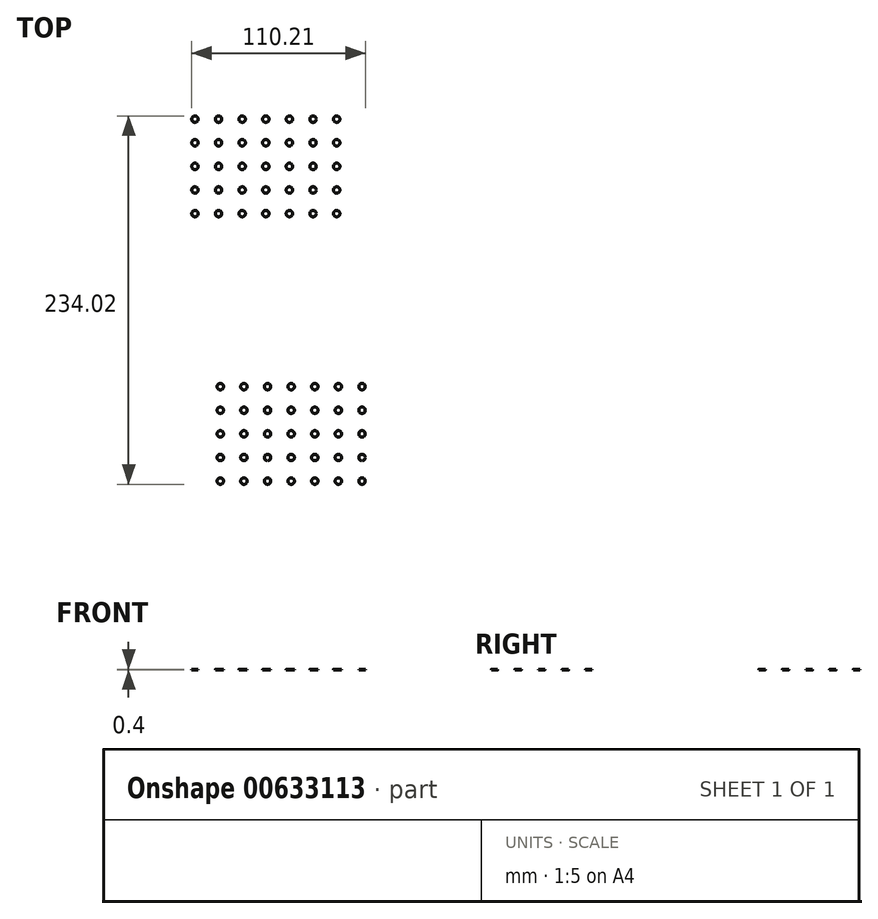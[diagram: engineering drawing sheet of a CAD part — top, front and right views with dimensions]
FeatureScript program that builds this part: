
annotation { "Feature Type Name" : "Feature", "Feature Type Description" : "" }
export const myFeature = defineFeature(function(context is Context, id is Id, definition is map)
    precondition{}
    {
        {
            var Q0;
            Q0=qCreatedBy(makeId("Top.planeOp"),FACE);
            var sketch = newSketch(context, id + "F0", { "sketchPlane" : qUnion([Q0])});
            skLineSegment(sketch, "E0.bottom", {"start": v(-80.56, 57.72) * mm, "end": v(79.44, 57.72) * mm});
            skLineSegment(sketch, "E0.right", {"start": v(79.44, 57.72) * mm, "end": v(79.44, -47.28) * mm});
            skCircle(sketch, "E1", {"center": v(-45.56, -24.78) * mm, "radius": 2.05 * mm});
            skCircle(sketch, "E2.0.1.0", {"center": v(-45.56, -9.78) * mm, "radius": 2.05 * mm});
            skCircle(sketch, "E2.0.2.0", {"center": v(-45.56, 5.22) * mm, "radius": 2.05 * mm});
            skCircle(sketch, "E2.0.3.0", {"center": v(-45.56, 20.22) * mm, "radius": 2.05 * mm});
            skCircle(sketch, "E2.1.0.0", {"center": v(-30.56, -24.78) * mm, "radius": 2.05 * mm});
            skCircle(sketch, "E2.1.1.0", {"center": v(-30.56, -9.78) * mm, "radius": 2.05 * mm});
            skCircle(sketch, "E2.1.2.0", {"center": v(-30.56, 5.22) * mm, "radius": 2.05 * mm});
            skCircle(sketch, "E2.1.3.0", {"center": v(-30.56, 20.22) * mm, "radius": 2.05 * mm});
            skCircle(sketch, "E2.2.0.0", {"center": v(-15.56, -24.78) * mm, "radius": 2.05 * mm});
            skCircle(sketch, "E2.2.1.0", {"center": v(-15.56, -9.78) * mm, "radius": 2.05 * mm});
            skCircle(sketch, "E2.2.2.0", {"center": v(-15.56, 5.22) * mm, "radius": 2.05 * mm});
            skCircle(sketch, "E2.2.3.0", {"center": v(-15.56, 20.22) * mm, "radius": 2.05 * mm});
            skCircle(sketch, "E2.3.0.0", {"center": v(-0.56, -24.78) * mm, "radius": 2.05 * mm});
            skCircle(sketch, "E2.3.1.0", {"center": v(-0.56, -9.78) * mm, "radius": 2.05 * mm});
            skCircle(sketch, "E2.3.2.0", {"center": v(-0.56, 5.22) * mm, "radius": 2.05 * mm});
            skCircle(sketch, "E2.3.3.0", {"center": v(-0.56, 20.22) * mm, "radius": 2.05 * mm});
            skCircle(sketch, "E2.4.0.0", {"center": v(14.44, -24.78) * mm, "radius": 2.05 * mm});
            skCircle(sketch, "E2.4.1.0", {"center": v(14.44, -9.78) * mm, "radius": 2.05 * mm});
            skCircle(sketch, "E2.4.2.0", {"center": v(14.44, 5.22) * mm, "radius": 2.05 * mm});
            skCircle(sketch, "E2.4.3.0", {"center": v(14.44, 20.22) * mm, "radius": 2.05 * mm});
            skCircle(sketch, "E2.5.0.0", {"center": v(29.44, -24.78) * mm, "radius": 2.05 * mm});
            skCircle(sketch, "E2.5.1.0", {"center": v(29.44, -9.78) * mm, "radius": 2.05 * mm});
            skCircle(sketch, "E2.5.2.0", {"center": v(29.44, 5.22) * mm, "radius": 2.05 * mm});
            skCircle(sketch, "E2.5.3.0", {"center": v(29.44, 20.22) * mm, "radius": 2.05 * mm});
            skCircle(sketch, "E2.6.0.0", {"center": v(44.44, -24.78) * mm, "radius": 2.05 * mm});
            skCircle(sketch, "E2.6.1.0", {"center": v(44.44, -9.78) * mm, "radius": 2.05 * mm});
            skCircle(sketch, "E2.6.2.0", {"center": v(44.44, 5.22) * mm, "radius": 2.05 * mm});
            skCircle(sketch, "E2.6.3.0", {"center": v(44.44, 20.22) * mm, "radius": 2.05 * mm});
            skLineSegment(sketch, "E2.direction1", {"start": v(-45.56, -24.78) * mm, "end": v(-30.56, -24.78) * mm, "construction": true});
            skLineSegment(sketch, "E2.direction2", {"start": v(-45.56, -24.78) * mm, "end": v(-45.56, -9.78) * mm, "construction": true});
            skCircle(sketch, "E3.0.0.4", {"center": v(-45.56, 35.22) * mm, "radius": 2.05 * mm});
            skCircle(sketch, "E3.0.1.4", {"center": v(-30.56, 35.22) * mm, "radius": 2.05 * mm});
            skCircle(sketch, "E3.0.2.4", {"center": v(-15.56, 35.22) * mm, "radius": 2.05 * mm});
            skCircle(sketch, "E3.0.3.4", {"center": v(-0.56, 35.22) * mm, "radius": 2.05 * mm});
            skCircle(sketch, "E3.0.4.4", {"center": v(14.44, 35.22) * mm, "radius": 2.05 * mm});
            skCircle(sketch, "E3.0.5.4", {"center": v(29.44, 35.22) * mm, "radius": 2.05 * mm});
            skCircle(sketch, "E3.0.6.4", {"center": v(44.44, 35.22) * mm, "radius": 2.05 * mm});
            skCircle(sketch, "E4", {"center": v(-70.56, 52.22) * mm, "radius": 1.55 * mm});
            skCircle(sketch, "E5", {"center": v(69.44, 52.22) * mm, "radius": 1.55 * mm});
            skCircle(sketch, "E6", {"center": v(-52.56, 52.22) * mm, "radius": 1.55 * mm});
            skCircle(sketch, "E7", {"center": v(51.44, 52.22) * mm, "radius": 1.55 * mm});
            skCircle(sketch, "E8", {"center": v(-45.56, 52.22) * mm, "radius": 2.6 * mm});
            skCircle(sketch, "E9", {"center": v(-0.56, 52.22) * mm, "radius": 2.6 * mm});
            skCircle(sketch, "E10", {"center": v(44.44, 52.22) * mm, "radius": 2.55 * mm});
            skCircle(sketch, "E11.MirrorC", {"center": v(-0.56, -41.78) * mm, "radius": 2.6 * mm});
            skCircle(sketch, "E12.MirrorC", {"center": v(51.44, -41.78) * mm, "radius": 1.55 * mm});
            skCircle(sketch, "E13.MirrorC", {"center": v(-52.56, -41.78) * mm, "radius": 1.55 * mm});
            skCircle(sketch, "E14.MirrorC", {"center": v(-45.56, -41.78) * mm, "radius": 2.6 * mm});
            skCircle(sketch, "E15.MirrorC", {"center": v(44.44, -41.78) * mm, "radius": 2.55 * mm});
            skCircle(sketch, "E16.MirrorC", {"center": v(69.44, -41.78) * mm, "radius": 1.55 * mm});
            skCircle(sketch, "E17.MirrorC", {"center": v(-70.56, -41.78) * mm, "radius": 1.55 * mm});
            skLineSegment(sketch, "E18.bottom", {"start": v(-64.45, -112.2) * mm, "end": v(95.55, -112.2) * mm});
            skLineSegment(sketch, "E18.right", {"start": v(95.55, -112.2) * mm, "end": v(95.55, -217.2) * mm});
            skCircle(sketch, "E19", {"center": v(-54.45, -117.7) * mm, "radius": 3 * mm});
            skCircle(sketch, "E20", {"center": v(85.55, -117.7) * mm, "radius": 3 * mm});
            skCircle(sketch, "E21", {"center": v(-36.45, -117.7) * mm, "radius": 1.55 * mm});
            skCircle(sketch, "E22", {"center": v(67.55, -117.7) * mm, "radius": 1.55 * mm});
            skCircle(sketch, "E23", {"center": v(-29.45, -117.7) * mm, "radius": 2.6 * mm});
            skCircle(sketch, "E24", {"center": v(15.55, -117.7) * mm, "radius": 2.6 * mm});
            skCircle(sketch, "E25", {"center": v(60.55, -117.7) * mm, "radius": 2.55 * mm});
            skLineSegment(sketch, "E26", {"start": v(95.55, -217.2) * mm, "end": v(15.55, -217.2) * mm});
            skCircle(sketch, "E27.MirrorC", {"center": v(15.55, -211.7) * mm, "radius": 2.6 * mm});
            skCircle(sketch, "E28.MirrorC", {"center": v(67.55, -211.7) * mm, "radius": 1.55 * mm});
            skCircle(sketch, "E29.MirrorC", {"center": v(-36.45, -211.7) * mm, "radius": 1.55 * mm});
            skCircle(sketch, "E30.MirrorC", {"center": v(-29.45, -211.7) * mm, "radius": 2.6 * mm});
            skCircle(sketch, "E31.MirrorC", {"center": v(60.55, -211.7) * mm, "radius": 2.55 * mm});
            skCircle(sketch, "E32.MirrorC", {"center": v(85.55, -211.7) * mm, "radius": 3 * mm});
            skCircle(sketch, "E33.MirrorC", {"center": v(-54.45, -211.7) * mm, "radius": 3 * mm});
            skCircle(sketch, "E34", {"center": v(-29.45, -194.7) * mm, "radius": 2.05 * mm});
            skCircle(sketch, "E35.0.1.0", {"center": v(-29.45, -179.7) * mm, "radius": 2.05 * mm});
            skCircle(sketch, "E35.0.2.0", {"center": v(-29.45, -164.7) * mm, "radius": 2.05 * mm});
            skCircle(sketch, "E35.0.3.0", {"center": v(-29.45, -149.7) * mm, "radius": 2.05 * mm});
            skCircle(sketch, "E35.1.0.0", {"center": v(-14.45, -194.7) * mm, "radius": 2.05 * mm});
            skCircle(sketch, "E35.1.1.0", {"center": v(-14.45, -179.7) * mm, "radius": 2.05 * mm});
            skCircle(sketch, "E35.1.2.0", {"center": v(-14.45, -164.7) * mm, "radius": 2.05 * mm});
            skCircle(sketch, "E35.1.3.0", {"center": v(-14.45, -149.7) * mm, "radius": 2.05 * mm});
            skCircle(sketch, "E35.2.0.0", {"center": v(0.55, -194.7) * mm, "radius": 2.05 * mm});
            skCircle(sketch, "E35.2.1.0", {"center": v(0.55, -179.7) * mm, "radius": 2.05 * mm});
            skCircle(sketch, "E35.2.2.0", {"center": v(0.55, -164.7) * mm, "radius": 2.05 * mm});
            skCircle(sketch, "E35.2.3.0", {"center": v(0.55, -149.7) * mm, "radius": 2.05 * mm});
            skCircle(sketch, "E35.3.0.0", {"center": v(15.55, -194.7) * mm, "radius": 2.05 * mm});
            skCircle(sketch, "E35.3.1.0", {"center": v(15.55, -179.7) * mm, "radius": 2.05 * mm});
            skCircle(sketch, "E35.3.2.0", {"center": v(15.55, -164.7) * mm, "radius": 2.05 * mm});
            skCircle(sketch, "E35.3.3.0", {"center": v(15.55, -149.7) * mm, "radius": 2.05 * mm});
            skCircle(sketch, "E35.4.0.0", {"center": v(30.55, -194.7) * mm, "radius": 2.05 * mm});
            skCircle(sketch, "E35.4.1.0", {"center": v(30.55, -179.7) * mm, "radius": 2.05 * mm});
            skCircle(sketch, "E35.4.2.0", {"center": v(30.55, -164.7) * mm, "radius": 2.05 * mm});
            skCircle(sketch, "E35.4.3.0", {"center": v(30.55, -149.7) * mm, "radius": 2.05 * mm});
            skCircle(sketch, "E35.5.0.0", {"center": v(45.55, -194.7) * mm, "radius": 2.05 * mm});
            skCircle(sketch, "E35.5.1.0", {"center": v(45.55, -179.7) * mm, "radius": 2.05 * mm});
            skCircle(sketch, "E35.5.2.0", {"center": v(45.55, -164.7) * mm, "radius": 2.05 * mm});
            skCircle(sketch, "E35.5.3.0", {"center": v(45.55, -149.7) * mm, "radius": 2.05 * mm});
            skCircle(sketch, "E35.6.0.0", {"center": v(60.55, -194.7) * mm, "radius": 2.05 * mm});
            skCircle(sketch, "E35.6.1.0", {"center": v(60.55, -179.7) * mm, "radius": 2.05 * mm});
            skCircle(sketch, "E35.6.2.0", {"center": v(60.55, -164.7) * mm, "radius": 2.05 * mm});
            skCircle(sketch, "E35.6.3.0", {"center": v(60.55, -149.7) * mm, "radius": 2.05 * mm});
            skLineSegment(sketch, "E35.direction1", {"start": v(-29.45, -194.7) * mm, "end": v(-14.45, -194.7) * mm, "construction": true});
            skLineSegment(sketch, "E35.direction2", {"start": v(-29.45, -194.7) * mm, "end": v(-29.45, -179.7) * mm, "construction": true});
            skCircle(sketch, "E36.0.0.4", {"center": v(-29.45, -134.7) * mm, "radius": 2.05 * mm});
            skCircle(sketch, "E36.0.1.4", {"center": v(-14.45, -134.7) * mm, "radius": 2.05 * mm});
            skCircle(sketch, "E36.0.2.4", {"center": v(0.55, -134.7) * mm, "radius": 2.05 * mm});
            skCircle(sketch, "E36.0.3.4", {"center": v(15.55, -134.7) * mm, "radius": 2.05 * mm});
            skCircle(sketch, "E36.0.4.4", {"center": v(30.55, -134.7) * mm, "radius": 2.05 * mm});
            skCircle(sketch, "E36.0.5.4", {"center": v(45.55, -134.7) * mm, "radius": 2.05 * mm});
            skCircle(sketch, "E36.0.6.4", {"center": v(60.55, -134.7) * mm, "radius": 2.05 * mm});
            skCircle(sketch, "E37", {"center": v(-61.56, 52.22) * mm, "radius": 3 * mm});
            skCircle(sketch, "E38", {"center": v(60.44, 52.22) * mm, "radius": 3 * mm});
            skCircle(sketch, "E39.MirrorC", {"center": v(60.44, -41.78) * mm, "radius": 3 * mm});
            skCircle(sketch, "E40.MirrorC", {"center": v(-61.56, -41.78) * mm, "radius": 3 * mm});
            skCircle(sketch, "E41", {"center": v(76.55, -117.7) * mm, "radius": 1.55 * mm});
            skCircle(sketch, "E42", {"center": v(-45.45, -117.7) * mm, "radius": 1.55 * mm});
            skCircle(sketch, "E43.MirrorC", {"center": v(-45.45, -211.7) * mm, "radius": 1.55 * mm});
            skCircle(sketch, "E44.MirrorC", {"center": v(76.55, -211.7) * mm, "radius": 1.55 * mm});
            skLineSegment(sketch, "E45", {"start": v(-80.56, 57.72) * mm, "end": v(-80.56, -47.28) * mm});
            skLineSegment(sketch, "E46", {"start": v(-80.56, -47.28) * mm, "end": v(79.44, -47.28) * mm});
            skLineSegment(sketch, "E47", {"start": v(-64.45, -112.2) * mm, "end": v(-64.45, -217.2) * mm});
            skLineSegment(sketch, "E48", {"start": v(-64.45, -217.2) * mm, "end": v(95.55, -217.2) * mm});
            skSolve(sketch);
        }
        {
            var Q0;
            Q0=makeQuery(id+"F0.imprint","IMPRINT",FACE,{"disambiguationData":[TD([[makeQuery(id+"F0.imprint","IMPRINT",EDGE,{"derivedFrom":sQuery(id+"F0.wireOp",EDGE,"E18.bottom")}),-1.0]])]});
            var sketch = newSketch(context, id + "F1", { "sketchPlane" : qUnion([Q0])});
            skSolve(sketch);
        }
        {
            var Q0;
            Q0=sQuery(id+"F0.wireOp",EDGE,"E45");
            var Q1;
            Q1=sQuery(id+"F0.wireOp",EDGE,"E46");
            var Q2;
            Q2=sQuery(id+"F0.wireOp",EDGE,"E0.right");
            var Q3;
            Q3=sQuery(id+"F0.wireOp",EDGE,"E0.bottom");
            var Q4;
            Q4=sQuery(id+"F0.wireOp",EDGE,"E18.bottom");
            var Q5;
            Q5=sQuery(id+"F0.wireOp",EDGE,"E47");
            var Q6;
            Q6=sQuery(id+"F0.wireOp",EDGE,"E48");
            var Q7;
            Q7=sQuery(id+"F0.wireOp",EDGE,"E18.right");
            extrude(context, id + "F2", {"bodyType" : ToolBodyType.SURFACE, "surfaceEntities" : qUnion([Q0, Q1, Q2, Q3, Q4, Q5, Q6, Q7]), "depth" : 5 * mm, "offsetDistance" : 25 * mm});
        }
        {
            var Q0;
            Q0=sQuery(id+"F0.wireOp",EDGE,"E20");
            var Q1;
            Q1=sQuery(id+"F0.wireOp",EDGE,"E41");
            var Q2;
            Q2=sQuery(id+"F0.wireOp",EDGE,"E22");
            var Q3;
            Q3=sQuery(id+"F0.wireOp",EDGE,"E25");
            var Q4;
            Q4=sQuery(id+"F0.wireOp",EDGE,"E24");
            var Q5;
            Q5=sQuery(id+"F0.wireOp",EDGE,"E23");
            var Q6;
            Q6=sQuery(id+"F0.wireOp",EDGE,"E21");
            var Q7;
            Q7=sQuery(id+"F0.wireOp",EDGE,"E42");
            var Q8;
            Q8=sQuery(id+"F0.wireOp",EDGE,"E19");
            extrude(context, id + "F3", {"bodyType" : ToolBodyType.SURFACE, "surfaceEntities" : qUnion([Q0, Q1, Q2, Q3, Q4, Q5, Q6, Q7, Q8]), "depth" : 5 * mm, "offsetDistance" : 25 * mm});
        }
        {
            var Q0;
            Q0=sQuery(id+"F0.wireOp",EDGE,"E33.MirrorC");
            var Q1;
            Q1=sQuery(id+"F0.wireOp",EDGE,"E43.MirrorC");
            var Q2;
            Q2=sQuery(id+"F0.wireOp",EDGE,"E29.MirrorC");
            var Q3;
            Q3=sQuery(id+"F0.wireOp",EDGE,"E30.MirrorC");
            var Q4;
            Q4=sQuery(id+"F0.wireOp",EDGE,"E27.MirrorC");
            var Q5;
            Q5=sQuery(id+"F0.wireOp",EDGE,"E31.MirrorC");
            var Q6;
            Q6=sQuery(id+"F0.wireOp",EDGE,"E28.MirrorC");
            var Q7;
            Q7=sQuery(id+"F0.wireOp",EDGE,"E44.MirrorC");
            var Q8;
            Q8=sQuery(id+"F0.wireOp",EDGE,"E32.MirrorC");
            extrude(context, id + "F4", {"bodyType" : ToolBodyType.SURFACE, "surfaceEntities" : qUnion([Q0, Q1, Q2, Q3, Q4, Q5, Q6, Q7, Q8]), "depth" : 5 * mm, "offsetDistance" : 25 * mm});
        }
        {
            var Q0;
            Q0=sQuery(id+"F0.wireOp",EDGE,"E4");
            var Q1;
            Q1=sQuery(id+"F0.wireOp",EDGE,"E37");
            var Q2;
            Q2=sQuery(id+"F0.wireOp",EDGE,"E6");
            var Q3;
            Q3=sQuery(id+"F0.wireOp",EDGE,"E8");
            var Q4;
            Q4=sQuery(id+"F0.wireOp",EDGE,"E9");
            var Q5;
            Q5=sQuery(id+"F0.wireOp",EDGE,"E10");
            var Q6;
            Q6=sQuery(id+"F0.wireOp",EDGE,"E7");
            var Q7;
            Q7=sQuery(id+"F0.wireOp",EDGE,"E38");
            var Q8;
            Q8=sQuery(id+"F0.wireOp",EDGE,"E5");
            extrude(context, id + "F5", {"bodyType" : ToolBodyType.SURFACE, "surfaceEntities" : qUnion([Q0, Q1, Q2, Q3, Q4, Q5, Q6, Q7, Q8]), "depth" : 5 * mm, "offsetDistance" : 25 * mm});
        }
        {
            var Q0;
            Q0=sQuery(id+"F0.wireOp",EDGE,"E17.MirrorC");
            var Q1;
            Q1=sQuery(id+"F0.wireOp",EDGE,"E40.MirrorC");
            var Q2;
            Q2=sQuery(id+"F0.wireOp",EDGE,"E13.MirrorC");
            var Q3;
            Q3=sQuery(id+"F0.wireOp",EDGE,"E14.MirrorC");
            var Q4;
            Q4=sQuery(id+"F0.wireOp",EDGE,"E11.MirrorC");
            var Q5;
            Q5=sQuery(id+"F0.wireOp",EDGE,"E15.MirrorC");
            var Q6;
            Q6=sQuery(id+"F0.wireOp",EDGE,"E12.MirrorC");
            var Q7;
            Q7=sQuery(id+"F0.wireOp",EDGE,"E39.MirrorC");
            var Q8;
            Q8=sQuery(id+"F0.wireOp",EDGE,"E16.MirrorC");
            extrude(context, id + "F6", {"bodyType" : ToolBodyType.SURFACE, "surfaceEntities" : qUnion([Q0, Q1, Q2, Q3, Q4, Q5, Q6, Q7, Q8]), "depth" : 5 * mm, "offsetDistance" : 25 * mm});
        }
        {
            var Q0;
            Q0=makeQuery(id+"F1.imprint","IMPRINT",FACE,{"disambiguationData":[TD([[makeQuery(id+"F1.imprint","IMPRINT",EDGE,{"derivedFrom":makeQuery(id+"F0.imprint","IMPRINT",EDGE,{"derivedFrom":sQuery(id+"F0.wireOp",EDGE,"E35.4.2.0")})}),1.0]])]});
            var Q1;
            Q1=makeQuery(id+"F1.imprint","IMPRINT",FACE,{"disambiguationData":[TD([[makeQuery(id+"F1.imprint","IMPRINT",EDGE,{"derivedFrom":makeQuery(id+"F0.imprint","IMPRINT",EDGE,{"derivedFrom":sQuery(id+"F0.wireOp",EDGE,"E36.0.4.4")})}),1.0]])]});
            var Q2;
            Q2=makeQuery(id+"F0.imprint","IMPRINT",FACE,{"disambiguationData":[TD([[makeQuery(id+"F0.imprint","IMPRINT",EDGE,{"derivedFrom":sQuery(id+"F0.wireOp",EDGE,"E35.5.1.0")}),1.0]])]});
            var Q3;
            Q3=makeQuery(id+"F1.imprint","IMPRINT",FACE,{"disambiguationData":[TD([[makeQuery(id+"F1.imprint","IMPRINT",EDGE,{"derivedFrom":makeQuery(id+"F0.imprint","IMPRINT",EDGE,{"derivedFrom":sQuery(id+"F0.wireOp",EDGE,"E35.6.2.0")})}),1.0]])]});
            var Q4;
            Q4=makeQuery(id+"F1.imprint","IMPRINT",FACE,{"disambiguationData":[TD([[makeQuery(id+"F1.imprint","IMPRINT",EDGE,{"derivedFrom":makeQuery(id+"F0.imprint","IMPRINT",EDGE,{"derivedFrom":sQuery(id+"F0.wireOp",EDGE,"E35.0.3.0")})}),1.0]])]});
            var Q5;
            Q5=makeQuery(id+"F1.imprint","IMPRINT",FACE,{"disambiguationData":[TD([[makeQuery(id+"F1.imprint","IMPRINT",EDGE,{"derivedFrom":makeQuery(id+"F0.imprint","IMPRINT",EDGE,{"derivedFrom":sQuery(id+"F0.wireOp",EDGE,"E35.1.3.0")})}),1.0]])]});
            var Q6;
            Q6=makeQuery(id+"F1.imprint","IMPRINT",FACE,{"disambiguationData":[TD([[makeQuery(id+"F1.imprint","IMPRINT",EDGE,{"derivedFrom":makeQuery(id+"F0.imprint","IMPRINT",EDGE,{"derivedFrom":sQuery(id+"F0.wireOp",EDGE,"E35.2.2.0")})}),1.0]])]});
            var Q7;
            Q7=makeQuery(id+"F1.imprint","IMPRINT",FACE,{"disambiguationData":[TD([[makeQuery(id+"F1.imprint","IMPRINT",EDGE,{"derivedFrom":makeQuery(id+"F0.imprint","IMPRINT",EDGE,{"derivedFrom":sQuery(id+"F0.wireOp",EDGE,"E36.0.3.4")})}),1.0]])]});
            var Q8;
            Q8=makeQuery(id+"F1.imprint","IMPRINT",FACE,{"disambiguationData":[TD([[makeQuery(id+"F1.imprint","IMPRINT",EDGE,{"derivedFrom":makeQuery(id+"F0.imprint","IMPRINT",EDGE,{"derivedFrom":sQuery(id+"F0.wireOp",EDGE,"E35.6.1.0")})}),1.0]])]});
            var Q9;
            Q9=makeQuery(id+"F1.imprint","IMPRINT",FACE,{"disambiguationData":[TD([[makeQuery(id+"F1.imprint","IMPRINT",EDGE,{"derivedFrom":makeQuery(id+"F0.imprint","IMPRINT",EDGE,{"derivedFrom":sQuery(id+"F0.wireOp",EDGE,"E36.0.6.4")})}),1.0]])]});
            var Q10;
            Q10=makeQuery(id+"F1.imprint","IMPRINT",FACE,{"disambiguationData":[TD([[makeQuery(id+"F1.imprint","IMPRINT",EDGE,{"derivedFrom":makeQuery(id+"F0.imprint","IMPRINT",EDGE,{"derivedFrom":sQuery(id+"F0.wireOp",EDGE,"E35.0.2.0")})}),1.0]])]});
            var Q11;
            Q11=makeQuery(id+"F1.imprint","IMPRINT",FACE,{"disambiguationData":[TD([[makeQuery(id+"F1.imprint","IMPRINT",EDGE,{"derivedFrom":makeQuery(id+"F0.imprint","IMPRINT",EDGE,{"derivedFrom":sQuery(id+"F0.wireOp",EDGE,"E35.2.1.0")})}),1.0]])]});
            var Q12;
            Q12=makeQuery(id+"F1.imprint","IMPRINT",FACE,{"disambiguationData":[TD([[makeQuery(id+"F1.imprint","IMPRINT",EDGE,{"derivedFrom":makeQuery(id+"F0.imprint","IMPRINT",EDGE,{"derivedFrom":sQuery(id+"F0.wireOp",EDGE,"E35.4.3.0")})}),1.0]])]});
            var Q13;
            Q13=makeQuery(id+"F0.imprint","IMPRINT",FACE,{"disambiguationData":[TD([[makeQuery(id+"F0.imprint","IMPRINT",EDGE,{"derivedFrom":sQuery(id+"F0.wireOp",EDGE,"E36.0.5.4")}),1.0]])]});
            var Q14;
            Q14=makeQuery(id+"F1.imprint","IMPRINT",FACE,{"disambiguationData":[TD([[makeQuery(id+"F1.imprint","IMPRINT",EDGE,{"derivedFrom":makeQuery(id+"F0.imprint","IMPRINT",EDGE,{"derivedFrom":sQuery(id+"F0.wireOp",EDGE,"E35.5.2.0")})}),1.0]])]});
            var Q15;
            Q15=makeQuery(id+"F0.imprint","IMPRINT",FACE,{"disambiguationData":[TD([[makeQuery(id+"F0.imprint","IMPRINT",EDGE,{"derivedFrom":sQuery(id+"F0.wireOp",EDGE,"E35.3.2.0")}),1.0]])]});
            var Q16;
            Q16=makeQuery(id+"F1.imprint","IMPRINT",FACE,{"disambiguationData":[TD([[makeQuery(id+"F1.imprint","IMPRINT",EDGE,{"derivedFrom":makeQuery(id+"F0.imprint","IMPRINT",EDGE,{"derivedFrom":sQuery(id+"F0.wireOp",EDGE,"E35.4.0.0")})}),1.0]])]});
            var Q17;
            Q17=makeQuery(id+"F1.imprint","IMPRINT",FACE,{"disambiguationData":[TD([[makeQuery(id+"F1.imprint","IMPRINT",EDGE,{"derivedFrom":makeQuery(id+"F0.imprint","IMPRINT",EDGE,{"derivedFrom":sQuery(id+"F0.wireOp",EDGE,"E36.0.1.4")})}),1.0]])]});
            var Q18;
            Q18=makeQuery(id+"F0.imprint","IMPRINT",FACE,{"disambiguationData":[TD([[makeQuery(id+"F0.imprint","IMPRINT",EDGE,{"derivedFrom":sQuery(id+"F0.wireOp",EDGE,"E35.4.1.0")}),1.0]])]});
            var Q19;
            Q19=makeQuery(id+"F0.imprint","IMPRINT",FACE,{"disambiguationData":[TD([[makeQuery(id+"F0.imprint","IMPRINT",EDGE,{"derivedFrom":sQuery(id+"F0.wireOp",EDGE,"E35.3.0.0")}),1.0]])]});
            var Q20;
            Q20=makeQuery(id+"F1.imprint","IMPRINT",FACE,{"disambiguationData":[TD([[makeQuery(id+"F1.imprint","IMPRINT",EDGE,{"derivedFrom":makeQuery(id+"F0.imprint","IMPRINT",EDGE,{"derivedFrom":sQuery(id+"F0.wireOp",EDGE,"E35.6.0.0")})}),1.0]])]});
            var Q21;
            Q21=makeQuery(id+"F0.imprint","IMPRINT",FACE,{"disambiguationData":[TD([[makeQuery(id+"F0.imprint","IMPRINT",EDGE,{"derivedFrom":sQuery(id+"F0.wireOp",EDGE,"E35.6.3.0")}),1.0]])]});
            var Q22;
            Q22=makeQuery(id+"F1.imprint","IMPRINT",FACE,{"disambiguationData":[TD([[makeQuery(id+"F1.imprint","IMPRINT",EDGE,{"derivedFrom":makeQuery(id+"F0.imprint","IMPRINT",EDGE,{"derivedFrom":sQuery(id+"F0.wireOp",EDGE,"E35.3.3.0")})}),1.0]])]});
            var Q23;
            Q23=makeQuery(id+"F1.imprint","IMPRINT",FACE,{"disambiguationData":[TD([[makeQuery(id+"F1.imprint","IMPRINT",EDGE,{"derivedFrom":makeQuery(id+"F0.imprint","IMPRINT",EDGE,{"derivedFrom":sQuery(id+"F0.wireOp",EDGE,"E35.2.0.0")})}),1.0]])]});
            var Q24;
            Q24=makeQuery(id+"F0.imprint","IMPRINT",FACE,{"disambiguationData":[TD([[makeQuery(id+"F0.imprint","IMPRINT",EDGE,{"derivedFrom":sQuery(id+"F0.wireOp",EDGE,"E35.1.1.0")}),1.0]])]});
            var Q25;
            Q25=makeQuery(id+"F0.imprint","IMPRINT",FACE,{"disambiguationData":[TD([[makeQuery(id+"F0.imprint","IMPRINT",EDGE,{"derivedFrom":sQuery(id+"F0.wireOp",EDGE,"E36.0.2.4")}),1.0]])]});
            var Q26;
            Q26=makeQuery(id+"F0.imprint","IMPRINT",FACE,{"disambiguationData":[TD([[makeQuery(id+"F0.imprint","IMPRINT",EDGE,{"derivedFrom":sQuery(id+"F0.wireOp",EDGE,"E36.0.0.4")}),1.0]])]});
            var Q27;
            Q27=makeQuery(id+"F0.imprint","IMPRINT",FACE,{"disambiguationData":[TD([[makeQuery(id+"F0.imprint","IMPRINT",EDGE,{"derivedFrom":sQuery(id+"F0.wireOp",EDGE,"E35.5.0.0")}),1.0]])]});
            var Q28;
            Q28=makeQuery(id+"F1.imprint","IMPRINT",FACE,{"disambiguationData":[TD([[makeQuery(id+"F1.imprint","IMPRINT",EDGE,{"derivedFrom":makeQuery(id+"F0.imprint","IMPRINT",EDGE,{"derivedFrom":sQuery(id+"F0.wireOp",EDGE,"E35.1.2.0")})}),1.0]])]});
            var Q29;
            Q29=makeQuery(id+"F1.imprint","IMPRINT",FACE,{"disambiguationData":[TD([[makeQuery(id+"F1.imprint","IMPRINT",EDGE,{"derivedFrom":makeQuery(id+"F0.imprint","IMPRINT",EDGE,{"derivedFrom":sQuery(id+"F0.wireOp",EDGE,"E35.3.1.0")})}),1.0]])]});
            var Q30;
            Q30=makeQuery(id+"F0.imprint","IMPRINT",FACE,{"disambiguationData":[TD([[makeQuery(id+"F0.imprint","IMPRINT",EDGE,{"derivedFrom":sQuery(id+"F0.wireOp",EDGE,"E35.2.3.0")}),1.0]])]});
            var Q31;
            Q31=makeQuery(id+"F1.imprint","IMPRINT",FACE,{"disambiguationData":[TD([[makeQuery(id+"F1.imprint","IMPRINT",EDGE,{"derivedFrom":makeQuery(id+"F0.imprint","IMPRINT",EDGE,{"derivedFrom":sQuery(id+"F0.wireOp",EDGE,"E35.5.3.0")})}),1.0]])]});
            var Q32;
            Q32=makeQuery(id+"F0.imprint","IMPRINT",FACE,{"disambiguationData":[TD([[makeQuery(id+"F0.imprint","IMPRINT",EDGE,{"derivedFrom":sQuery(id+"F0.wireOp",EDGE,"E36.0.1.4")}),1.0]])]});
            var Q33;
            Q33=makeQuery(id+"F0.imprint","IMPRINT",FACE,{"disambiguationData":[TD([[makeQuery(id+"F0.imprint","IMPRINT",EDGE,{"derivedFrom":sQuery(id+"F0.wireOp",EDGE,"E35.2.0.0")}),1.0]])]});
            var Q34;
            Q34=makeQuery(id+"F0.imprint","IMPRINT",FACE,{"disambiguationData":[TD([[makeQuery(id+"F0.imprint","IMPRINT",EDGE,{"derivedFrom":sQuery(id+"F0.wireOp",EDGE,"E35.0.2.0")}),1.0]])]});
            var Q35;
            Q35=makeQuery(id+"F1.imprint","IMPRINT",FACE,{"disambiguationData":[TD([[makeQuery(id+"F1.imprint","IMPRINT",EDGE,{"derivedFrom":makeQuery(id+"F0.imprint","IMPRINT",EDGE,{"derivedFrom":sQuery(id+"F0.wireOp",EDGE,"E35.6.3.0")})}),1.0]])]});
            var Q36;
            Q36=makeQuery(id+"F0.imprint","IMPRINT",FACE,{"disambiguationData":[TD([[makeQuery(id+"F0.imprint","IMPRINT",EDGE,{"derivedFrom":sQuery(id+"F0.wireOp",EDGE,"E35.0.3.0")}),1.0]])]});
            var Q37;
            Q37=makeQuery(id+"F0.imprint","IMPRINT",FACE,{"disambiguationData":[TD([[makeQuery(id+"F0.imprint","IMPRINT",EDGE,{"derivedFrom":sQuery(id+"F0.wireOp",EDGE,"E35.6.1.0")}),1.0]])]});
            var Q38;
            Q38=makeQuery(id+"F0.imprint","IMPRINT",FACE,{"disambiguationData":[TD([[makeQuery(id+"F0.imprint","IMPRINT",EDGE,{"derivedFrom":sQuery(id+"F0.wireOp",EDGE,"E36.0.3.4")}),1.0]])]});
            var Q39;
            Q39=makeQuery(id+"F1.imprint","IMPRINT",FACE,{"disambiguationData":[TD([[makeQuery(id+"F1.imprint","IMPRINT",EDGE,{"derivedFrom":makeQuery(id+"F0.imprint","IMPRINT",EDGE,{"derivedFrom":sQuery(id+"F0.wireOp",EDGE,"E36.0.2.4")})}),1.0]])]});
            var Q40;
            Q40=makeQuery(id+"F0.imprint","IMPRINT",FACE,{"disambiguationData":[TD([[makeQuery(id+"F0.imprint","IMPRINT",EDGE,{"derivedFrom":sQuery(id+"F0.wireOp",EDGE,"E35.4.3.0")}),1.0]])]});
            var Q41;
            Q41=makeQuery(id+"F0.imprint","IMPRINT",FACE,{"disambiguationData":[TD([[makeQuery(id+"F0.imprint","IMPRINT",EDGE,{"derivedFrom":sQuery(id+"F0.wireOp",EDGE,"E35.3.1.0")}),1.0]])]});
            var Q42;
            Q42=makeQuery(id+"F1.imprint","IMPRINT",FACE,{"disambiguationData":[TD([[makeQuery(id+"F1.imprint","IMPRINT",EDGE,{"derivedFrom":makeQuery(id+"F0.imprint","IMPRINT",EDGE,{"derivedFrom":sQuery(id+"F0.wireOp",EDGE,"E36.0.0.4")})}),1.0]])]});
            var Q43;
            Q43=makeQuery(id+"F0.imprint","IMPRINT",FACE,{"disambiguationData":[TD([[makeQuery(id+"F0.imprint","IMPRINT",EDGE,{"derivedFrom":sQuery(id+"F0.wireOp",EDGE,"E35.5.3.0")}),1.0]])]});
            var Q44;
            Q44=makeQuery(id+"F1.imprint","IMPRINT",FACE,{"disambiguationData":[TD([[makeQuery(id+"F1.imprint","IMPRINT",EDGE,{"derivedFrom":makeQuery(id+"F0.imprint","IMPRINT",EDGE,{"derivedFrom":sQuery(id+"F0.wireOp",EDGE,"E35.4.1.0")})}),1.0]])]});
            var Q45;
            Q45=makeQuery(id+"F0.imprint","IMPRINT",FACE,{"disambiguationData":[TD([[makeQuery(id+"F0.imprint","IMPRINT",EDGE,{"derivedFrom":sQuery(id+"F0.wireOp",EDGE,"E35.0.1.0")}),1.0]])]});
            var Q46;
            Q46=makeQuery(id+"F1.imprint","IMPRINT",FACE,{"disambiguationData":[TD([[makeQuery(id+"F1.imprint","IMPRINT",EDGE,{"derivedFrom":makeQuery(id+"F0.imprint","IMPRINT",EDGE,{"derivedFrom":sQuery(id+"F0.wireOp",EDGE,"E35.2.3.0")})}),1.0]])]});
            var Q47;
            Q47=makeQuery(id+"F1.imprint","IMPRINT",FACE,{"disambiguationData":[TD([[makeQuery(id+"F1.imprint","IMPRINT",EDGE,{"derivedFrom":makeQuery(id+"F0.imprint","IMPRINT",EDGE,{"derivedFrom":sQuery(id+"F0.wireOp",EDGE,"E35.5.1.0")})}),1.0]])]});
            var Q48;
            Q48=makeQuery(id+"F1.imprint","IMPRINT",FACE,{"disambiguationData":[TD([[makeQuery(id+"F1.imprint","IMPRINT",EDGE,{"derivedFrom":makeQuery(id+"F0.imprint","IMPRINT",EDGE,{"derivedFrom":sQuery(id+"F0.wireOp",EDGE,"E35.5.0.0")})}),1.0]])]});
            var Q49;
            Q49=makeQuery(id+"F0.imprint","IMPRINT",FACE,{"disambiguationData":[TD([[makeQuery(id+"F0.imprint","IMPRINT",EDGE,{"derivedFrom":sQuery(id+"F0.wireOp",EDGE,"E35.4.2.0")}),1.0]])]});
            var Q50;
            Q50=makeQuery(id+"F0.imprint","IMPRINT",FACE,{"disambiguationData":[TD([[makeQuery(id+"F0.imprint","IMPRINT",EDGE,{"derivedFrom":sQuery(id+"F0.wireOp",EDGE,"E35.3.3.0")}),1.0]])]});
            var Q51;
            Q51=makeQuery(id+"F0.imprint","IMPRINT",FACE,{"disambiguationData":[TD([[makeQuery(id+"F0.imprint","IMPRINT",EDGE,{"derivedFrom":sQuery(id+"F0.wireOp",EDGE,"E35.6.0.0")}),1.0]])]});
            var Q52;
            Q52=makeQuery(id+"F0.imprint","IMPRINT",FACE,{"disambiguationData":[TD([[makeQuery(id+"F0.imprint","IMPRINT",EDGE,{"derivedFrom":sQuery(id+"F0.wireOp",EDGE,"E35.1.3.0")}),1.0]])]});
            var Q53;
            Q53=makeQuery(id+"F0.imprint","IMPRINT",FACE,{"disambiguationData":[TD([[makeQuery(id+"F0.imprint","IMPRINT",EDGE,{"derivedFrom":sQuery(id+"F0.wireOp",EDGE,"E35.1.0.0")}),1.0]])]});
            var Q54;
            Q54=makeQuery(id+"F1.imprint","IMPRINT",FACE,{"disambiguationData":[TD([[makeQuery(id+"F1.imprint","IMPRINT",EDGE,{"derivedFrom":makeQuery(id+"F0.imprint","IMPRINT",EDGE,{"derivedFrom":sQuery(id+"F0.wireOp",EDGE,"E35.3.2.0")})}),1.0]])]});
            var Q55;
            Q55=makeQuery(id+"F0.imprint","IMPRINT",FACE,{"disambiguationData":[TD([[makeQuery(id+"F0.imprint","IMPRINT",EDGE,{"derivedFrom":sQuery(id+"F0.wireOp",EDGE,"E35.5.2.0")}),1.0]])]});
            var Q56;
            Q56=makeQuery(id+"F0.imprint","IMPRINT",FACE,{"disambiguationData":[TD([[makeQuery(id+"F0.imprint","IMPRINT",EDGE,{"derivedFrom":sQuery(id+"F0.wireOp",EDGE,"E36.0.6.4")}),1.0]])]});
            var Q57;
            Q57=makeQuery(id+"F0.imprint","IMPRINT",FACE,{"disambiguationData":[TD([[makeQuery(id+"F0.imprint","IMPRINT",EDGE,{"derivedFrom":sQuery(id+"F0.wireOp",EDGE,"E35.4.0.0")}),1.0]])]});
            var Q58;
            Q58=makeQuery(id+"F0.imprint","IMPRINT",FACE,{"disambiguationData":[TD([[makeQuery(id+"F0.imprint","IMPRINT",EDGE,{"derivedFrom":sQuery(id+"F0.wireOp",EDGE,"E35.1.2.0")}),1.0]])]});
            var Q59;
            Q59=makeQuery(id+"F0.imprint","IMPRINT",FACE,{"disambiguationData":[TD([[makeQuery(id+"F0.imprint","IMPRINT",EDGE,{"derivedFrom":sQuery(id+"F0.wireOp",EDGE,"E36.0.4.4")}),1.0]])]});
            var Q60;
            Q60=makeQuery(id+"F1.imprint","IMPRINT",FACE,{"disambiguationData":[TD([[makeQuery(id+"F1.imprint","IMPRINT",EDGE,{"derivedFrom":makeQuery(id+"F0.imprint","IMPRINT",EDGE,{"derivedFrom":sQuery(id+"F0.wireOp",EDGE,"E35.3.0.0")})}),1.0]])]});
            var Q61;
            Q61=makeQuery(id+"F0.imprint","IMPRINT",FACE,{"disambiguationData":[TD([[makeQuery(id+"F0.imprint","IMPRINT",EDGE,{"derivedFrom":sQuery(id+"F0.wireOp",EDGE,"E35.6.2.0")}),1.0]])]});
            var Q62;
            Q62=makeQuery(id+"F1.imprint","IMPRINT",FACE,{"disambiguationData":[TD([[makeQuery(id+"F1.imprint","IMPRINT",EDGE,{"derivedFrom":makeQuery(id+"F0.imprint","IMPRINT",EDGE,{"derivedFrom":sQuery(id+"F0.wireOp",EDGE,"E36.0.5.4")})}),1.0]])]});
            var Q63;
            Q63=makeQuery(id+"F0.imprint","IMPRINT",FACE,{"disambiguationData":[TD([[makeQuery(id+"F0.imprint","IMPRINT",EDGE,{"derivedFrom":sQuery(id+"F0.wireOp",EDGE,"E35.2.1.0")}),1.0]])]});
            var Q64;
            Q64=makeQuery(id+"F1.imprint","IMPRINT",FACE,{"disambiguationData":[TD([[makeQuery(id+"F1.imprint","IMPRINT",EDGE,{"derivedFrom":makeQuery(id+"F0.imprint","IMPRINT",EDGE,{"derivedFrom":sQuery(id+"F0.wireOp",EDGE,"E35.1.1.0")})}),1.0]])]});
            var Q65;
            Q65=makeQuery(id+"F0.imprint","IMPRINT",FACE,{"disambiguationData":[TD([[makeQuery(id+"F0.imprint","IMPRINT",EDGE,{"derivedFrom":sQuery(id+"F0.wireOp",EDGE,"E35.2.2.0")}),1.0]])]});
            var Q66;
            Q66=makeQuery(id+"F1.imprint","IMPRINT",FACE,{"disambiguationData":[TD([[makeQuery(id+"F1.imprint","IMPRINT",EDGE,{"derivedFrom":makeQuery(id+"F0.imprint","IMPRINT",EDGE,{"derivedFrom":sQuery(id+"F0.wireOp",EDGE,"E35.1.0.0")})}),1.0]])]});
            var Q67;
            Q67=makeQuery(id+"F1.imprint","IMPRINT",FACE,{"disambiguationData":[TD([[makeQuery(id+"F1.imprint","IMPRINT",EDGE,{"derivedFrom":makeQuery(id+"F0.imprint","IMPRINT",EDGE,{"derivedFrom":sQuery(id+"F0.wireOp",EDGE,"E35.0.1.0")})}),1.0]])]});
            var Q68;
            Q68=makeQuery(id+"F1.imprint","IMPRINT",FACE,{"disambiguationData":[TD([[makeQuery(id+"F1.imprint","IMPRINT",EDGE,{"derivedFrom":makeQuery(id+"F0.imprint","IMPRINT",EDGE,{"derivedFrom":sQuery(id+"F0.wireOp",EDGE,"E34")})}),1.0]])]});
            var Q69;
            Q69=makeQuery(id+"F0.imprint","IMPRINT",FACE,{"disambiguationData":[TD([[makeQuery(id+"F0.imprint","IMPRINT",EDGE,{"derivedFrom":sQuery(id+"F0.wireOp",EDGE,"E34")}),1.0]])]});
            extrude(context, id + "F7", {"entities" : qUnion([Q0, Q1, Q2, Q3, Q4, Q5, Q6, Q7, Q8, Q9, Q10, Q11, Q12, Q13, Q14, Q15, Q16, Q17, Q18, Q19, Q20, Q21, Q22, Q23, Q24, Q25, Q26, Q27, Q28, Q29, Q30, Q31, Q32, Q33, Q34, Q35, Q36, Q37, Q38, Q39, Q40, Q41, Q42, Q43, Q44, Q45, Q46, Q47, Q48, Q49, Q50, Q51, Q52, Q53, Q54, Q55, Q56, Q57, Q58, Q59, Q60, Q61, Q62, Q63, Q64, Q65, Q66, Q67, Q68, Q69]), "depth" : 0.4 * mm, "offsetDistance" : 25 * mm});
        }
        {
            var Q0;
            Q0=makeQuery(id+"F0.imprint","IMPRINT",FACE,{"disambiguationData":[TD([[makeQuery(id+"F0.imprint","IMPRINT",EDGE,{"derivedFrom":sQuery(id+"F0.wireOp",EDGE,"E2.6.2.0")}),1.0]])]});
            var Q1;
            Q1=makeQuery(id+"F0.imprint","IMPRINT",FACE,{"disambiguationData":[TD([[makeQuery(id+"F0.imprint","IMPRINT",EDGE,{"derivedFrom":sQuery(id+"F0.wireOp",EDGE,"E3.0.1.4")}),1.0]])]});
            var Q2;
            Q2=makeQuery(id+"F0.imprint","IMPRINT",FACE,{"disambiguationData":[TD([[makeQuery(id+"F0.imprint","IMPRINT",EDGE,{"derivedFrom":sQuery(id+"F0.wireOp",EDGE,"E2.6.3.0")}),1.0]])]});
            var Q3;
            Q3=makeQuery(id+"F0.imprint","IMPRINT",FACE,{"disambiguationData":[TD([[makeQuery(id+"F0.imprint","IMPRINT",EDGE,{"derivedFrom":sQuery(id+"F0.wireOp",EDGE,"E3.0.2.4")}),1.0]])]});
            var Q4;
            Q4=makeQuery(id+"F0.imprint","IMPRINT",FACE,{"disambiguationData":[TD([[makeQuery(id+"F0.imprint","IMPRINT",EDGE,{"derivedFrom":sQuery(id+"F0.wireOp",EDGE,"E3.0.0.4")}),1.0]])]});
            var Q5;
            Q5=makeQuery(id+"F0.imprint","IMPRINT",FACE,{"disambiguationData":[TD([[makeQuery(id+"F0.imprint","IMPRINT",EDGE,{"derivedFrom":sQuery(id+"F0.wireOp",EDGE,"E2.4.0.0")}),1.0]])]});
            var Q6;
            Q6=makeQuery(id+"F0.imprint","IMPRINT",FACE,{"disambiguationData":[TD([[makeQuery(id+"F0.imprint","IMPRINT",EDGE,{"derivedFrom":sQuery(id+"F0.wireOp",EDGE,"E3.0.4.4")}),1.0]])]});
            var Q7;
            Q7=makeQuery(id+"F0.imprint","IMPRINT",FACE,{"disambiguationData":[TD([[makeQuery(id+"F0.imprint","IMPRINT",EDGE,{"derivedFrom":sQuery(id+"F0.wireOp",EDGE,"E2.4.1.0")}),1.0]])]});
            var Q8;
            Q8=makeQuery(id+"F0.imprint","IMPRINT",FACE,{"disambiguationData":[TD([[makeQuery(id+"F0.imprint","IMPRINT",EDGE,{"derivedFrom":sQuery(id+"F0.wireOp",EDGE,"E3.0.5.4")}),1.0]])]});
            var Q9;
            Q9=makeQuery(id+"F0.imprint","IMPRINT",FACE,{"disambiguationData":[TD([[makeQuery(id+"F0.imprint","IMPRINT",EDGE,{"derivedFrom":sQuery(id+"F0.wireOp",EDGE,"E2.4.2.0")}),1.0]])]});
            var Q10;
            Q10=makeQuery(id+"F0.imprint","IMPRINT",FACE,{"disambiguationData":[TD([[makeQuery(id+"F0.imprint","IMPRINT",EDGE,{"derivedFrom":sQuery(id+"F0.wireOp",EDGE,"E3.0.6.4")}),1.0]])]});
            var Q11;
            Q11=makeQuery(id+"F0.imprint","IMPRINT",FACE,{"disambiguationData":[TD([[makeQuery(id+"F0.imprint","IMPRINT",EDGE,{"derivedFrom":sQuery(id+"F0.wireOp",EDGE,"E2.4.3.0")}),1.0]])]});
            var Q12;
            Q12=makeQuery(id+"F0.imprint","IMPRINT",FACE,{"disambiguationData":[TD([[makeQuery(id+"F0.imprint","IMPRINT",EDGE,{"derivedFrom":sQuery(id+"F0.wireOp",EDGE,"E2.5.0.0")}),1.0]])]});
            var Q13;
            Q13=makeQuery(id+"F0.imprint","IMPRINT",FACE,{"disambiguationData":[TD([[makeQuery(id+"F0.imprint","IMPRINT",EDGE,{"derivedFrom":sQuery(id+"F0.wireOp",EDGE,"E2.5.1.0")}),1.0]])]});
            var Q14;
            Q14=makeQuery(id+"F0.imprint","IMPRINT",FACE,{"disambiguationData":[TD([[makeQuery(id+"F0.imprint","IMPRINT",EDGE,{"derivedFrom":sQuery(id+"F0.wireOp",EDGE,"E2.5.2.0")}),1.0]])]});
            var Q15;
            Q15=makeQuery(id+"F0.imprint","IMPRINT",FACE,{"disambiguationData":[TD([[makeQuery(id+"F0.imprint","IMPRINT",EDGE,{"derivedFrom":sQuery(id+"F0.wireOp",EDGE,"E2.3.3.0")}),1.0]])]});
            var Q16;
            Q16=makeQuery(id+"F0.imprint","IMPRINT",FACE,{"disambiguationData":[TD([[makeQuery(id+"F0.imprint","IMPRINT",EDGE,{"derivedFrom":sQuery(id+"F0.wireOp",EDGE,"E2.3.1.0")}),1.0]])]});
            var Q17;
            Q17=makeQuery(id+"F0.imprint","IMPRINT",FACE,{"disambiguationData":[TD([[makeQuery(id+"F0.imprint","IMPRINT",EDGE,{"derivedFrom":sQuery(id+"F0.wireOp",EDGE,"E2.3.2.0")}),1.0]])]});
            var Q18;
            Q18=makeQuery(id+"F0.imprint","IMPRINT",FACE,{"disambiguationData":[TD([[makeQuery(id+"F0.imprint","IMPRINT",EDGE,{"derivedFrom":sQuery(id+"F0.wireOp",EDGE,"E1")}),1.0]])]});
            var Q19;
            Q19=makeQuery(id+"F0.imprint","IMPRINT",FACE,{"disambiguationData":[TD([[makeQuery(id+"F0.imprint","IMPRINT",EDGE,{"derivedFrom":sQuery(id+"F0.wireOp",EDGE,"E2.0.1.0")}),1.0]])]});
            var Q20;
            Q20=makeQuery(id+"F0.imprint","IMPRINT",FACE,{"disambiguationData":[TD([[makeQuery(id+"F0.imprint","IMPRINT",EDGE,{"derivedFrom":sQuery(id+"F0.wireOp",EDGE,"E2.0.2.0")}),1.0]])]});
            var Q21;
            Q21=makeQuery(id+"F0.imprint","IMPRINT",FACE,{"disambiguationData":[TD([[makeQuery(id+"F0.imprint","IMPRINT",EDGE,{"derivedFrom":sQuery(id+"F0.wireOp",EDGE,"E2.0.3.0")}),1.0]])]});
            var Q22;
            Q22=makeQuery(id+"F0.imprint","IMPRINT",FACE,{"disambiguationData":[TD([[makeQuery(id+"F0.imprint","IMPRINT",EDGE,{"derivedFrom":sQuery(id+"F0.wireOp",EDGE,"E2.1.0.0")}),1.0]])]});
            var Q23;
            Q23=makeQuery(id+"F0.imprint","IMPRINT",FACE,{"disambiguationData":[TD([[makeQuery(id+"F0.imprint","IMPRINT",EDGE,{"derivedFrom":sQuery(id+"F0.wireOp",EDGE,"E2.1.1.0")}),1.0]])]});
            var Q24;
            Q24=makeQuery(id+"F0.imprint","IMPRINT",FACE,{"disambiguationData":[TD([[makeQuery(id+"F0.imprint","IMPRINT",EDGE,{"derivedFrom":sQuery(id+"F0.wireOp",EDGE,"E2.1.2.0")}),1.0]])]});
            var Q25;
            Q25=makeQuery(id+"F0.imprint","IMPRINT",FACE,{"disambiguationData":[TD([[makeQuery(id+"F0.imprint","IMPRINT",EDGE,{"derivedFrom":sQuery(id+"F0.wireOp",EDGE,"E2.1.3.0")}),1.0]])]});
            var Q26;
            Q26=makeQuery(id+"F0.imprint","IMPRINT",FACE,{"disambiguationData":[TD([[makeQuery(id+"F0.imprint","IMPRINT",EDGE,{"derivedFrom":sQuery(id+"F0.wireOp",EDGE,"E2.2.0.0")}),1.0]])]});
            var Q27;
            Q27=makeQuery(id+"F0.imprint","IMPRINT",FACE,{"disambiguationData":[TD([[makeQuery(id+"F0.imprint","IMPRINT",EDGE,{"derivedFrom":sQuery(id+"F0.wireOp",EDGE,"E2.2.1.0")}),1.0]])]});
            var Q28;
            Q28=makeQuery(id+"F0.imprint","IMPRINT",FACE,{"disambiguationData":[TD([[makeQuery(id+"F0.imprint","IMPRINT",EDGE,{"derivedFrom":sQuery(id+"F0.wireOp",EDGE,"E2.2.2.0")}),1.0]])]});
            var Q29;
            Q29=makeQuery(id+"F0.imprint","IMPRINT",FACE,{"disambiguationData":[TD([[makeQuery(id+"F0.imprint","IMPRINT",EDGE,{"derivedFrom":sQuery(id+"F0.wireOp",EDGE,"E2.2.3.0")}),1.0]])]});
            var Q30;
            Q30=makeQuery(id+"F0.imprint","IMPRINT",FACE,{"disambiguationData":[TD([[makeQuery(id+"F0.imprint","IMPRINT",EDGE,{"derivedFrom":sQuery(id+"F0.wireOp",EDGE,"E2.3.0.0")}),1.0]])]});
            var Q31;
            Q31=makeQuery(id+"F0.imprint","IMPRINT",FACE,{"disambiguationData":[TD([[makeQuery(id+"F0.imprint","IMPRINT",EDGE,{"derivedFrom":sQuery(id+"F0.wireOp",EDGE,"E2.5.3.0")}),1.0]])]});
            var Q32;
            Q32=makeQuery(id+"F0.imprint","IMPRINT",FACE,{"disambiguationData":[TD([[makeQuery(id+"F0.imprint","IMPRINT",EDGE,{"derivedFrom":sQuery(id+"F0.wireOp",EDGE,"E2.6.0.0")}),1.0]])]});
            var Q33;
            Q33=makeQuery(id+"F0.imprint","IMPRINT",FACE,{"disambiguationData":[TD([[makeQuery(id+"F0.imprint","IMPRINT",EDGE,{"derivedFrom":sQuery(id+"F0.wireOp",EDGE,"E3.0.3.4")}),1.0]])]});
            var Q34;
            Q34=makeQuery(id+"F0.imprint","IMPRINT",FACE,{"disambiguationData":[TD([[makeQuery(id+"F0.imprint","IMPRINT",EDGE,{"derivedFrom":sQuery(id+"F0.wireOp",EDGE,"E2.6.1.0")}),1.0]])]});
            extrude(context, id + "F8", {"entities" : qUnion([Q0, Q1, Q2, Q3, Q4, Q5, Q6, Q7, Q8, Q9, Q10, Q11, Q12, Q13, Q14, Q15, Q16, Q17, Q18, Q19, Q20, Q21, Q22, Q23, Q24, Q25, Q26, Q27, Q28, Q29, Q30, Q31, Q32, Q33, Q34]), "depth" : 0.4 * mm, "offsetDistance" : 25 * mm});
        }
    });
